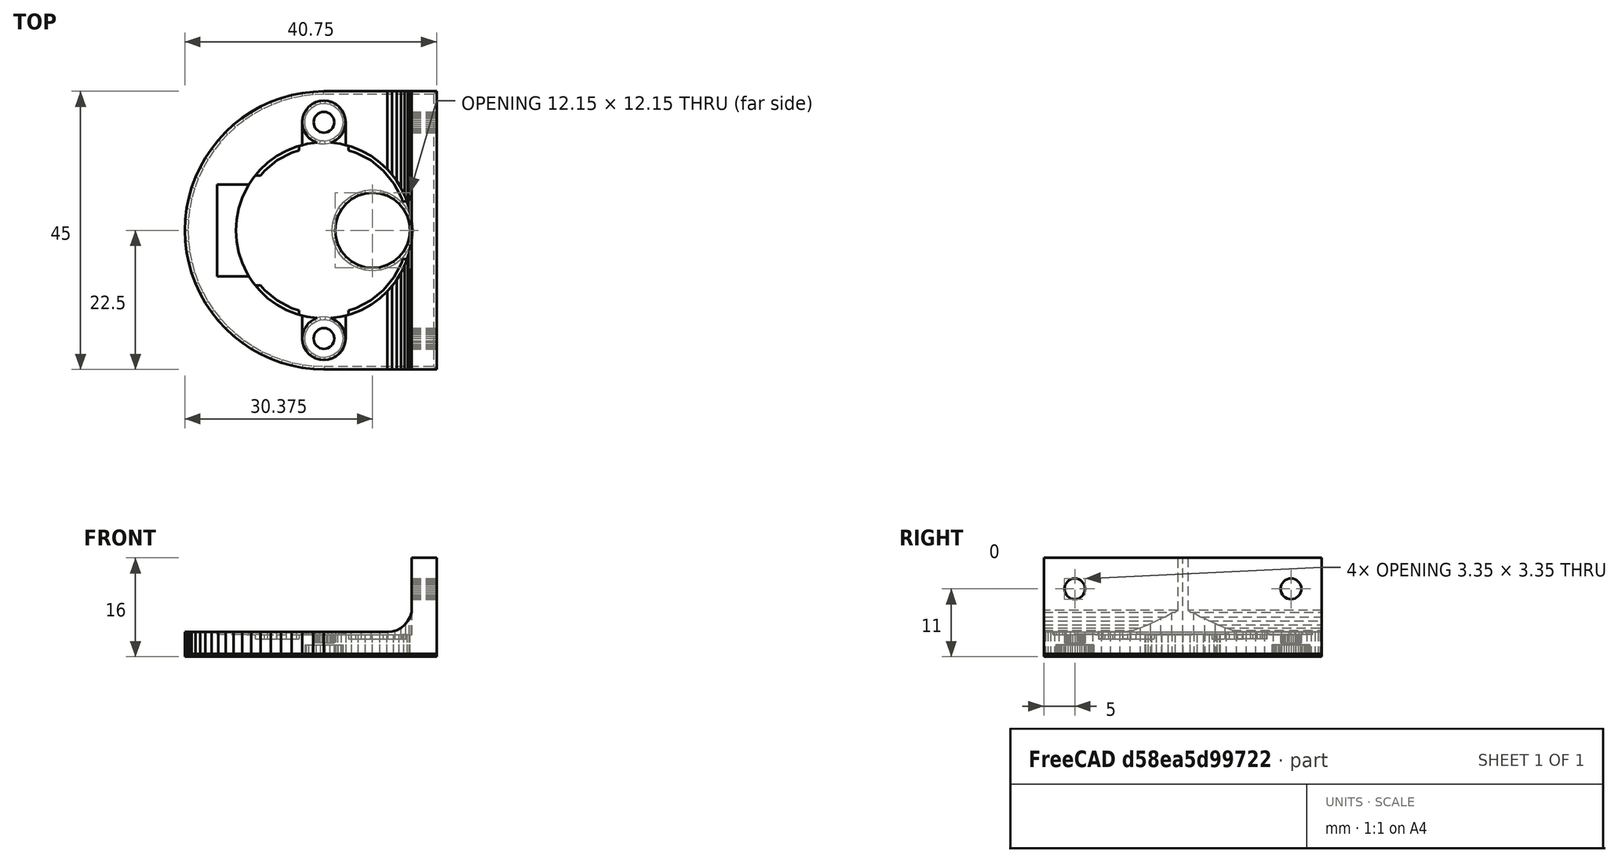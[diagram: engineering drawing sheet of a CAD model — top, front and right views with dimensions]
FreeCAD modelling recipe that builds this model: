
FCSTD DOCUMENT  (FreeCAD 0.14R3692 (Git))
Label: Bracket_28BYJ-48
License: CC-BY 3.0
LicenseURL: http://creativecommons.org/licenses/by/3.0/
objects: Part::Prism×18, Part::Box×9, Part::Cut×5, Part::MultiFuse×4, Part::Feature×4, Part::Fuse×2, PartDesign::Chamfer×1
note: 43 computed .brp shape members not serialized (recipe doc carries the construction recipe); baked Part::Feature solids carry a one-line shape summary decoded from their .brp

FEATURE [Part::Prism] prism
  Circumradius = 22.5
  Height = 4
  Placement = pos=(0,0,-2) rot=(0,0,1;0rad)
  Polygon = 80
FEATURE [Part::Box] cube
  Height = 16
  Length = 4.05
  Placement = pos=(14.2,-22.5,-14) rot=(0,0,1;0rad)
  Width = 45
FEATURE [Part::Box] cube001
  Height = 4
  Length = 45
  Placement = pos=(0,-22.5,-2) rot=(0,0,1;0rad)
  Width = 45
FEATURE [Part::Prism] prism001
  Circumradius = 4
  Height = 45
  Polygon = 32
FEATURE [Part::Prism] prism002
  Circumradius = 4
  Height = 45
  Placement = pos=(-4,-4,0) rot=(0,0,1;0rad)
  Polygon = 32
FEATURE [Part::Cut] difference
  Base = -> prism001
  Placement = pos=(14.25,22.5,-2) rot=(1,0,0;1.5708rad)
  Tool = -> prism002
FEATURE [Part::MultiFuse] union
  Shapes = -> [prism,cube,cube001,difference]
FEATURE [Part::Box] cube002
  Height = 57
  Length = 57
  Placement = pos=(18.25,-28.5,-28.5) rot=(0,0,1;0rad)
  Width = 57
FEATURE [Part::Prism] prism003
  Circumradius = 1.675
  Height = 30
  Placement = pos=(0,17.5,-30.25) rot=(0,0,1;0rad)
  Polygon = 32
FEATURE [Part::Prism] prism004
  Circumradius = 1.675
  Height = 30
  Placement = pos=(0,-17.5,-30.25) rot=(0,0,1;0rad)
  Polygon = 32
FEATURE [Part::Prism] prism005
  Circumradius = 1.675
  Height = 30
  Placement = pos=(-5,17.5,-9) rot=(0,1,0;1.5708rad)
  Polygon = 32
FEATURE [Part::Prism] prism006
  Circumradius = 1.675
  Height = 30
  Placement = pos=(-5,-17.5,-9) rot=(0,1,0;1.5708rad)
  Polygon = 32
FEATURE [Part::Prism] prism007
  Circumradius = 3.075
  Height = 2
  Placement = pos=(0,17.5,0.05) rot=(0,0,1;0rad)
  Polygon = 25
FEATURE [Part::Prism] prism008
  Circumradius = 3.075
  Height = 2
  Placement = pos=(0,-17.5,0.05) rot=(0,0,1;0rad)
  Polygon = 25
FEATURE [Part::Prism] prism009
  Circumradius = 14.25
  Height = 0.75
  Placement = pos=(0,0,-0.375) rot=(0,0,1;0rad)
  Polygon = 50
FEATURE [Part::Prism] prism010
  Circumradius = 13.625
  Height = 0.8
  Placement = pos=(0,0,-0.4) rot=(0,0,1;0rad)
  Polygon = 32
FEATURE [Part::Box] cube003
  Height = 1.4
  Length = 8
  Placement = pos=(-4,-17.5,-0.7) rot=(0,0,1;0rad)
  Width = 35
FEATURE [Part::Box] cube004
  Height = 1.4
  Length = 31
  Placement = pos=(-15.5,-4.675,-0.7) rot=(0,0,1;0rad)
  Width = 9.35
FEATURE [Part::Box] cube005
  Height = 1.4
  Length = 28.5
  Placement = pos=(-28.5,-8.9,-0.7) rot=(0,0,1;0rad)
  Width = 17.8
FEATURE [Part::MultiFuse] union001
  Shapes = -> [prism010,cube003,cube004,cube005]
FEATURE [Part::Cut] difference001
  Base = -> prism009
  Placement = pos=(0,0,-9.75) rot=(0,0,1;0rad)
  Tool = -> union001
FEATURE [Part::Prism] prism011
  Circumradius = 14.25
  Height = 18.8
  Placement = pos=(0,0,-9.4) rot=(0,0,1;0rad)
  Polygon = 50
FEATURE [Part::Prism] prism012
  Circumradius = 4.675
  Height = 18.8
  Placement = pos=(7.875,0,-10.85) rot=(0,0,1;0rad)
  Polygon = 32
FEATURE [Part::Prism] prism013
  Circumradius = 6.075
  Height = 18.8
  Placement = pos=(0,0,-9.4) rot=(0,0,1;0rad)
  Polygon = 32
FEATURE [Part::Feature] emptycube
  Placement = pos=(1.5,-6.075,-9.425) rot=(0,0,1;0rad)
FEATURE [Part::Feature] emptycube001
  Placement = pos=(-13.65,-6.075,-9.425) rot=(0,0,1;0rad)
FEATURE [Part::Fuse] union002
  Base = -> emptycube
  Tool = -> emptycube001
FEATURE [Part::Cut] difference002
  Base = -> prism013
  Placement = pos=(7.875,0,-9.75) rot=(0,0,1;0rad)
  Tool = -> union002
FEATURE [Part::Box] cube006
  Height = 0.8
  Length = 7
  Placement = pos=(-3.5,-17.5,-9.375) rot=(0,0,1;0rad)
  Width = 35
FEATURE [Part::Prism] prism014
  Circumradius = 3.5
  Height = 0.8
  Placement = pos=(0,17.5,-9.4) rot=(0,0,1;0rad)
  Polygon = 32
FEATURE [Part::Prism] prism015
  Circumradius = 3.5
  Height = 0.8
  Placement = pos=(0,-17.5,-9.4) rot=(0,0,1;0rad)
  Polygon = 32
FEATURE [Part::Box] cube007
  Height = 16.7
  Length = 28.5
  Placement = pos=(-17.3,-7.425,-9.35) rot=(0,0,1;0rad)
  Width = 14.85
FEATURE [Part::Box] cube008
  Height = 15
  Length = 24.5
  Placement = pos=(-14.25,-8,-7.5) rot=(0,0,1;0rad)
  Width = 16
FEATURE [Part::MultiFuse] union003
  Shapes = -> [difference001,prism011,prism012,difference002,cube006,prism014,prism015,cube007,cube008]
FEATURE [Part::Prism] prism016
  Circumradius = 1.5
  Height = 2
  Placement = pos=(0,17.5,-10.4) rot=(0,0,1;0rad)
  Polygon = 32
FEATURE [Part::Prism] prism017
  Circumradius = 1.5
  Height = 2
  Placement = pos=(0,-17.5,-10.4) rot=(0,0,1;0rad)
  Polygon = 32
FEATURE [Part::Fuse] union004
  Base = -> prism016
  Tool = -> prism017
FEATURE [Part::Cut] difference003
  Base = -> union003
  Placement = pos=(0,0,-11) rot=(1,0,0;3.14159rad)
  Tool = -> union004
FEATURE [Part::MultiFuse] union005
  Shapes = -> [cube002,prism003,prism004,prism005,prism006,prism007,prism008,difference003]
FEATURE [Part::Cut] difference004  label="OpenSCAD_Model"
  Base = -> union
  Placement = pos=(0,0,0) rot=(1,0,0;3.14159rad)
  Tool = -> union005
FEATURE [Part::Feature] difference004001  label="OpenSCAD_Model (RefineShape)"
  shape: bbox 40.75 x 45 x 16 mm, 431 faces (baked)
FEATURE [PartDesign::Chamfer] Chamfer  label="PrintingChamfer"
  Base = -> difference004001 [Edge509,Edge512,Edge516,Edge519,Edge522,Edge525,Edge528,Edge531,Edge534,Edge537,Edge540,Edge543,Edge546,Edge549,Edge552,Edge555,Edge558,Edge561,Edge564,Edge567,Edge570,Edge573,Edge576,Edge579,Edge582,Edge585,Edge588,Edge591,Edge594,Edge597,Edge600,Edge603,Edge606,Edge609,Edge612,Edge615,Edge618,Edge621,Edge624,Edge627,+85 more]
  Size = 0.5
FEATURE [Part::Feature] Chamfer001  label="Bracket_28BYJ-48"
  shape: bbox 40.87 x 45.12 x 16.12 mm, 556 faces (baked)
